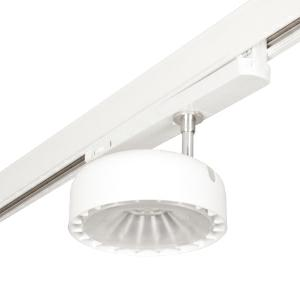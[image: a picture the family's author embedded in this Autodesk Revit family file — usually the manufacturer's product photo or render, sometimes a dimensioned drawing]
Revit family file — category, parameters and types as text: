
# Revit family: 3f_filippi_-_3f_emilio_track_ellittico_3f_filippi_-_47619_-_3f_emilio_tk_led_3000-930_ell
name_source: partatom
category: Lighting Fixtures
units: mm (PartAtom-declared; Revit-internal decimal feet)

## family parameters
Cut with Voids When Loaded = No
Host = Face
Light Source = No
Part Type = Normal
Room Calculation Point = No
Round Connector Dimension = Use Diameter
Shared = No

## types (1)
- 3F Filippi - 3F Emilio Track Ellittico (1 x LED, 2994 lm, 35 W, 3000 K)
    Apparent Load = 35 VA
    Approval mark = CE
    CIE Flux Codes = 85 95 99 100 100
    Color Rendering = 90
    Color Temperature = 3000 K
    Control Gear = Electronic ballast
    Default Elevation = 1800 mm
    Description = Adjustable spot light with minimal dimensions for accent lighting, to be integrated into the busbar.

ILLUMINOTECHNICAL
Luminous efficiency 100% (DLOR 100%, ULOR 0%).
Initial luminous flux of the luminaire 2994 lm.
Symmetrical and elliptical distribution.
Tabular UGR (CIE 117 - 4H-8H; S=0.25H; 70/50/20): RUG 21.3 - 26.
Beam angle: 42° - 87°.
Luminous efficacy 86 lm/W.
Lifetime (L90/B20): 30000 h. (tq+25°C)
Lifetime (L80/B20): 50000 h. (tq+25°C)
Sudden decreased luminous flux after 50000 hours: 0% (C0).
Photobiological safety in compliance with IEC/TR 62778: RG1 low risk, (IEC 62471).
In compliance with IEC/EN 62722-2-1 - IEC/EN 62717 standards.

SOURCE
Compact LED module 3000/930.
Energy efficiency class (UE 2019/2020 - UE 2019/2015): F.
CIE 13.3 Colour rendering index: CRI >90 (R9 >50%).
IES TM-30 Fidelity Index: Rf = 92 Rg = 101.
CCT nominal colour temperature 3000 K.
Colour initial tolerance (MacAdam): SDCM 3.
Zhaga Book 3 compliant.

MECHANICAL
Wired unit in white polycarbonate with busbar adaptor.
Single-piece in die-cast aluminium with passive dissipation, white colour, with perimeter cooling slots on upper edge, giving a crown of light effect to the fitting.
Invisible lock for positioning the luminous flux.
Lens made from transparent methacrylate (PMMA) with glossy surface and differentiated photo-etched.
Positioning arm in galvanised brass with sphere to allow for vertical positioning at angles from 0° to 90° and horizontal positioning from 0° to 290°.
Dimensions: diameter 130 mm, length 230 mm, height 105 mm. Weight 0.825 kg.
IP20 protection degree.
Glow-wire test resistance 650°C.

ELECTRICAL
Wiring unit separate from the body, invisible and integrated into the busbar.
Halogen Free electronic wiring 230V-50/60Hz, power factor 0.95, THD <25%, constant output current, SELV, class II, 1 driver.
Power of the luminaire 35 W.
ENEC - CE.
SAFE FLICKER: PstLM=<1 and SVM=<0.4 (IEC TR 61547-1 and IEC TR 63158), to ensure a more comfortable and safe light.
Ambient temperature from 0°C to +25°C.
Temperature class T6 max 85°C.
Relative humidity UR: <85%.

INSTALLATION
Track.

APPLICATIONS
Transit areas, spotlighting in commercial environments, exhibition areas, restaurants, shops and shop windows.

WARNING
Luminaire designed for disposal/recycling at end-of-life.
Replaceable (LED only) light source by a professional. Replaceable control gear by a professional.
    Height = 105 mm
    Lamp = 1 x LED
    Lamp Light Flux = 2994 lm
    Lamp Power = 35 W
    Lamp count = 1
    Length = 230 mm
    Lifetime = 50000 h
    Luminous efficacy = 86 lm/W
    Manufacturer = 3F Filippi
    ModVariant = No
    Model = 3F Filippi - 47619 - 3F Emilio TK LED 3000-930 ELL
    Mounting Place = Ceiling
    Mounting Type = Rail mounted
    Number of Poles = 1
    OnlyDefault = Yes
    Power Factor = 1
    Product Name = 3F Filippi - 3F Emilio Track Ellittico
    Product group = track mounted spotlight
    ProductGroupID = 12
    Protection Class = Protection class II
    Protection Degree = IP 20
    RLX_Detail_Level = 1
    RLX_Emergency_Light_Flux = 0 lm
    RLX_Emergency_Type = 0
    RLX_Emergency_Type_DB = No
    RlxData = <blob elided: 152253 chars, md5=ab548696>
    Socket = socket
    Standby Power = 0 W
    System Light Flux = 2994 lm
    System Power = 35 W
    Type Comments = Product without accessories
    Type Image = 3ffilippi_47619.jpg
    URL = http://relux.com
    VarID = ---
    Voltage = 0 V
    Weight = 0.00 kg
    Width = 130 mm

## geometry (parser evidence)
native form markers: Blend x4, Sweep x15
no freeform markers — native parametric forms only
